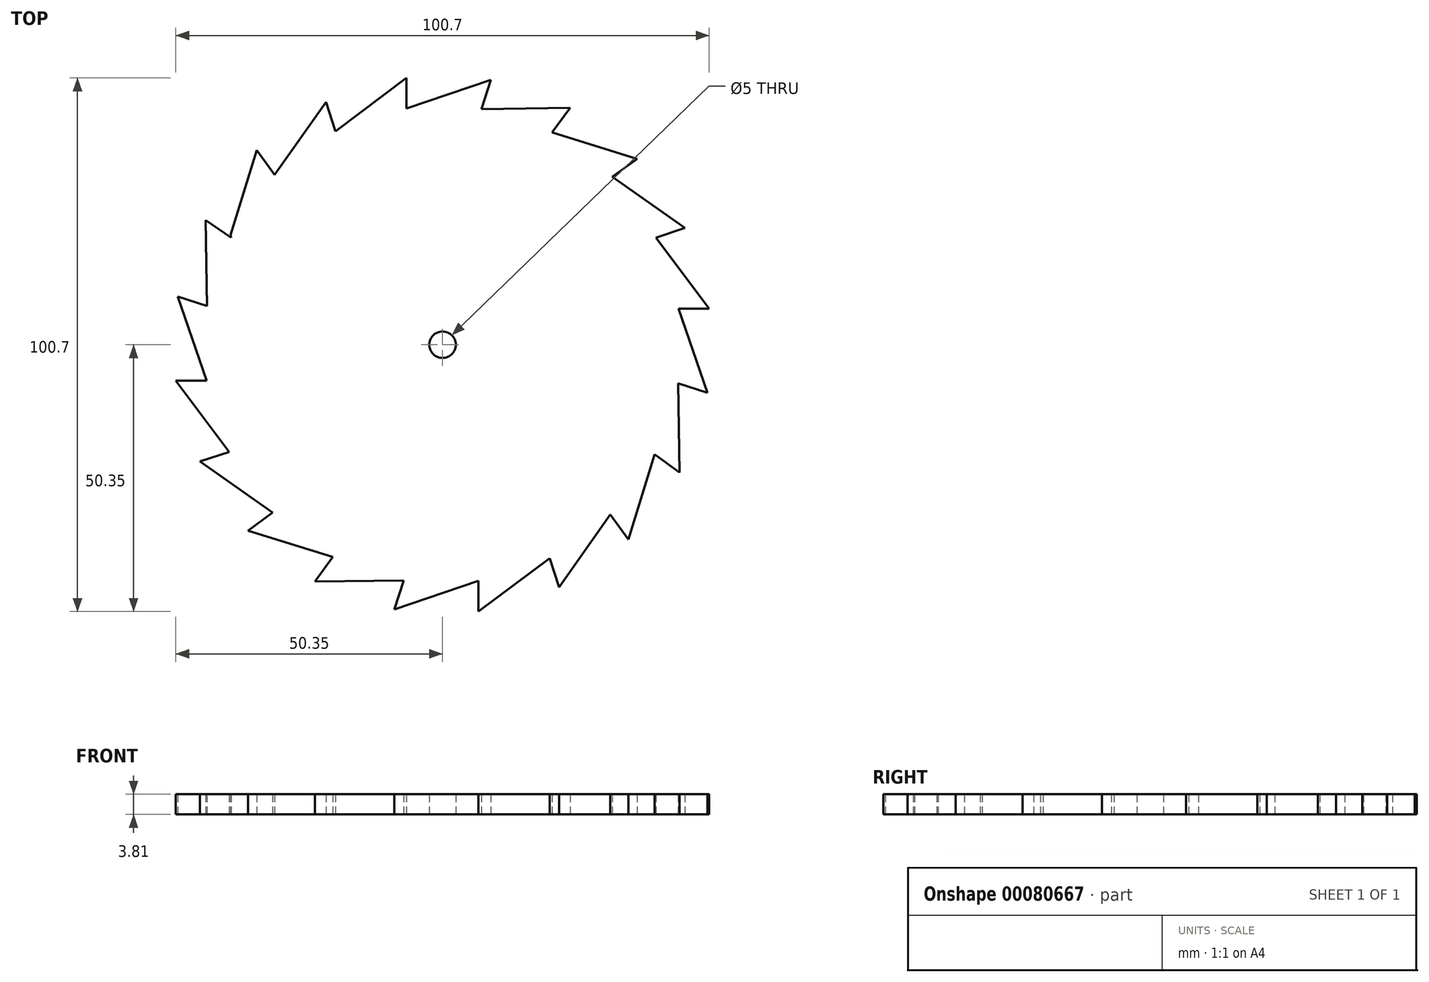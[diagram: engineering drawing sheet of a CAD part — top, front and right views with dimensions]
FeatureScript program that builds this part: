
annotation { "Feature Type Name" : "Feature", "Feature Type Description" : "" }
export const myFeature = defineFeature(function(context is Context, id is Id, definition is map)
    precondition{}
    {
        {
            var Q0;
            Q0=qCreatedBy(makeId("Top.planeOp"),FACE);
            var sketch = newSketch(context, id + "F0", { "sketchPlane" : qUnion([Q0])});
            skCircle(sketch, "E0", {"center": v(0, 0) * mm, "radius": 2.5 * mm});
            skCircle(sketch, "E1", {"center": v(0, 0) * mm, "radius": 8.48 * mm});
            skArc(sketch, "E2", {"start": v(-36.74, -35.09) * mm, "mid": v(-32.76, -38.83) * mm, "end": v(-28.4, -42.13) * mm});
            skLineSegment(sketch, "E3", {"start": v(0, 50.8) * mm, "end": v(-6.8, 44.57) * mm});
            skLineSegment(sketch, "E4", {"start": v(-6.8, 44.57) * mm, "end": v(-6.8, 50.35) * mm});
            skLineSegment(sketch, "E5.1.0", {"start": v(-17.4, 47.73) * mm, "end": v(-20.23, 40.29) * mm});
            skLineSegment(sketch, "E5.1.2", {"start": v(-20.23, 40.29) * mm, "end": v(-22.02, 45.78) * mm});
            skLineSegment(sketch, "E5.2.0", {"start": v(-31.3, 40.02) * mm, "end": v(-31.7, 32.06) * mm});
            skLineSegment(sketch, "E5.2.2", {"start": v(-31.7, 32.06) * mm, "end": v(-35.09, 36.74) * mm});
            skLineSegment(sketch, "E5.3.0", {"start": v(-42.13, 28.4) * mm, "end": v(-39.92, 20.21) * mm});
            skLineSegment(sketch, "E5.3.2", {"start": v(-39.92, 20.21) * mm, "end": v(-44.95, 23.67) * mm});
            skLineSegment(sketch, "E5.4.0", {"start": v(-48.84, 13.99) * mm, "end": v(-44.48, 7.31) * mm});
            skLineSegment(sketch, "E5.4.2", {"start": v(-44.48, 7.31) * mm, "end": v(-49.98, 9.1) * mm});
            skLineSegment(sketch, "E5.5.0", {"start": v(-50.77, -1.8) * mm, "end": v(-44.57, -6.8) * mm});
            skLineSegment(sketch, "E5.5.2", {"start": v(-44.57, -6.8) * mm, "end": v(-50.35, -6.8) * mm});
            skLineSegment(sketch, "E5.6.0", {"start": v(-47.73, -17.4) * mm, "end": v(-40.29, -20.23) * mm});
            skLineSegment(sketch, "E5.6.2", {"start": v(-40.29, -20.23) * mm, "end": v(-45.78, -22.02) * mm});
            skLineSegment(sketch, "E5.7.0", {"start": v(-40.02, -31.3) * mm, "end": v(-32.06, -31.7) * mm});
            skLineSegment(sketch, "E5.7.2", {"start": v(-32.06, -31.7) * mm, "end": v(-36.74, -35.09) * mm});
            skLineSegment(sketch, "E5.8.0", {"start": v(-28.4, -42.13) * mm, "end": v(-20.7, -40.05) * mm});
            skLineSegment(sketch, "E5.8.2", {"start": v(-20.7, -40.05) * mm, "end": v(-24.1, -44.72) * mm});
            skLineSegment(sketch, "E5.9.0", {"start": v(-13.99, -48.84) * mm, "end": v(-7.31, -44.48) * mm});
            skLineSegment(sketch, "E5.9.2", {"start": v(-7.31, -44.48) * mm, "end": v(-9.1, -49.98) * mm});
            skLineSegment(sketch, "E5.10.0", {"start": v(1.8, -50.77) * mm, "end": v(6.8, -44.57) * mm});
            skLineSegment(sketch, "E5.10.2", {"start": v(6.8, -44.57) * mm, "end": v(6.8, -50.35) * mm});
            skLineSegment(sketch, "E5.11.0", {"start": v(17.4, -47.73) * mm, "end": v(20.23, -40.29) * mm});
            skLineSegment(sketch, "E5.11.2", {"start": v(20.23, -40.29) * mm, "end": v(22.02, -45.78) * mm});
            skLineSegment(sketch, "E5.12.0", {"start": v(31.3, -40.02) * mm, "end": v(31.7, -32.06) * mm});
            skLineSegment(sketch, "E5.12.2", {"start": v(31.7, -32.06) * mm, "end": v(35.09, -36.74) * mm});
            skLineSegment(sketch, "E5.13.0", {"start": v(42.13, -28.4) * mm, "end": v(40.05, -20.7) * mm});
            skLineSegment(sketch, "E5.13.2", {"start": v(40.05, -20.7) * mm, "end": v(44.72, -24.1) * mm});
            skLineSegment(sketch, "E5.14.0", {"start": v(48.84, -13.99) * mm, "end": v(44.48, -7.31) * mm});
            skLineSegment(sketch, "E5.14.2", {"start": v(44.48, -7.31) * mm, "end": v(49.98, -9.1) * mm});
            skLineSegment(sketch, "E5.15.0", {"start": v(50.77, 1.8) * mm, "end": v(44.57, 6.8) * mm});
            skLineSegment(sketch, "E5.15.2", {"start": v(44.57, 6.8) * mm, "end": v(50.35, 6.8) * mm});
            skLineSegment(sketch, "E5.16.0", {"start": v(47.73, 17.4) * mm, "end": v(40.29, 20.23) * mm});
            skLineSegment(sketch, "E5.16.2", {"start": v(40.29, 20.23) * mm, "end": v(45.78, 22.02) * mm});
            skLineSegment(sketch, "E5.17.0", {"start": v(40.02, 31.3) * mm, "end": v(32.06, 31.7) * mm});
            skLineSegment(sketch, "E5.17.2", {"start": v(32.06, 31.7) * mm, "end": v(36.74, 35.09) * mm});
            skLineSegment(sketch, "E5.18.0", {"start": v(28.4, 42.13) * mm, "end": v(20.7, 40.05) * mm});
            skLineSegment(sketch, "E5.18.2", {"start": v(20.7, 40.05) * mm, "end": v(24.1, 44.72) * mm});
            skLineSegment(sketch, "E5.19.0", {"start": v(13.99, 48.84) * mm, "end": v(7.31, 44.48) * mm});
            skLineSegment(sketch, "E5.19.2", {"start": v(7.31, 44.48) * mm, "end": v(9.1, 49.98) * mm});
            skArc(sketch, "E6.trimOffspring", {"start": v(-9.1, -49.98) * mm, "mid": v(-3.67, -50.67) * mm, "end": v(1.8, -50.77) * mm});
            skArc(sketch, "E7.trimOffspring", {"start": v(-24.1, -44.72) * mm, "mid": v(-19.15, -47.06) * mm, "end": v(-13.99, -48.84) * mm});
            skArc(sketch, "E8.trimOffspring", {"start": v(-6.8, 50.35) * mm, "mid": v(-12.16, 49.33) * mm, "end": v(-17.4, 47.73) * mm});
            skArc(sketch, "E9.trimOffspring", {"start": v(-22.02, 45.78) * mm, "mid": v(-26.81, 43.15) * mm, "end": v(-31.3, 40.02) * mm});
            skArc(sketch, "E10.trimOffspring", {"start": v(-35.09, 36.74) * mm, "mid": v(-38.83, 32.76) * mm, "end": v(-42.13, 28.4) * mm});
            skArc(sketch, "E11.trimOffspring", {"start": v(-44.95, 23.67) * mm, "mid": v(-47.15, 18.93) * mm, "end": v(-48.84, 13.99) * mm});
            skArc(sketch, "E12.trimOffspring", {"start": v(-49.98, 9.1) * mm, "mid": v(-50.67, 3.67) * mm, "end": v(-50.77, -1.8) * mm});
            skArc(sketch, "E13.trimOffspring", {"start": v(-50.35, -6.8) * mm, "mid": v(-49.33, -12.16) * mm, "end": v(-47.73, -17.4) * mm});
            skArc(sketch, "E14.trimOffspring", {"start": v(-45.78, -22.02) * mm, "mid": v(-43.15, -26.81) * mm, "end": v(-40.02, -31.3) * mm});
            skArc(sketch, "E15.trimOffspring", {"start": v(6.8, -50.35) * mm, "mid": v(12.16, -49.33) * mm, "end": v(17.4, -47.73) * mm});
            skArc(sketch, "E16.trimOffspring", {"start": v(22.02, -45.78) * mm, "mid": v(26.81, -43.15) * mm, "end": v(31.3, -40.02) * mm});
            skArc(sketch, "E17.trimOffspring", {"start": v(35.09, -36.74) * mm, "mid": v(38.83, -32.76) * mm, "end": v(42.13, -28.4) * mm});
            skArc(sketch, "E18.trimOffspring", {"start": v(44.72, -24.1) * mm, "mid": v(47.06, -19.15) * mm, "end": v(48.84, -13.99) * mm});
            skArc(sketch, "E19.trimOffspring", {"start": v(49.98, -9.1) * mm, "mid": v(50.67, -3.67) * mm, "end": v(50.77, 1.8) * mm});
            skArc(sketch, "E20.trimOffspring", {"start": v(50.35, 6.8) * mm, "mid": v(49.33, 12.16) * mm, "end": v(47.73, 17.4) * mm});
            skArc(sketch, "E21.trimOffspring", {"start": v(45.78, 22.02) * mm, "mid": v(43.15, 26.81) * mm, "end": v(40.02, 31.3) * mm});
            skArc(sketch, "E22.trimOffspring", {"start": v(36.74, 35.09) * mm, "mid": v(32.76, 38.83) * mm, "end": v(28.4, 42.13) * mm});
            skArc(sketch, "E23.trimOffspring", {"start": v(24.1, 44.72) * mm, "mid": v(19.15, 47.06) * mm, "end": v(13.99, 48.84) * mm});
            skArc(sketch, "E24.trimOffspring", {"start": v(9.1, 49.98) * mm, "mid": v(4.57, 50.6) * mm, "end": v(0, 50.8) * mm});
            skPoint(sketch, "E25.orphan", {"position": v(-5.14, -35.84) * mm});
            skPoint(sketch, "E26.orphan", {"position": v(6.8, -32.02) * mm});
            skPoint(sketch, "E27.orphan", {"position": v(16.9, -32.02) * mm});
            skPoint(sketch, "E28.orphan", {"position": v(25.97, -25.23) * mm});
            skPoint(sketch, "E29.orphan", {"position": v(32.5, -15.97) * mm});
            skPoint(sketch, "E30.orphan", {"position": v(35.84, -5.14) * mm});
            skPoint(sketch, "E31.orphan", {"position": v(-29.9, 13.33) * mm});
            skPoint(sketch, "E32.orphan", {"position": v(-24.32, 21.91) * mm});
            skPoint(sketch, "E33.orphan", {"position": v(-16.35, 28.35) * mm});
            skPoint(sketch, "E34.orphan", {"position": v(-6.8, 32.02) * mm});
            skPoint(sketch, "E35.orphan", {"position": v(13.33, 29.9) * mm});
            skPoint(sketch, "E36.orphan", {"position": v(35.68, 6.18) * mm});
            skPoint(sketch, "E37.orphan", {"position": v(32.02, 16.9) * mm});
            skLineSegment(sketch, "E38", {"start": v(-22.02, 45.78) * mm, "end": v(-31.7, 32.06) * mm});
            skLineSegment(sketch, "E39.1.0", {"start": v(-35.09, 36.74) * mm, "end": v(-40.05, 20.7) * mm});
            skLineSegment(sketch, "E39.2.0", {"start": v(-44.72, 24.1) * mm, "end": v(-44.48, 7.31) * mm});
            skLineSegment(sketch, "E39.3.0", {"start": v(-49.98, 9.1) * mm, "end": v(-44.57, -6.8) * mm});
            skLineSegment(sketch, "E39.4.0", {"start": v(-50.35, -6.8) * mm, "end": v(-40.29, -20.23) * mm});
            skLineSegment(sketch, "E39.5.0", {"start": v(-45.78, -22.02) * mm, "end": v(-32.06, -31.7) * mm});
            skLineSegment(sketch, "E39.6.0", {"start": v(-36.74, -35.09) * mm, "end": v(-20.7, -40.05) * mm});
            skLineSegment(sketch, "E39.7.0", {"start": v(-24.1, -44.72) * mm, "end": v(-7.31, -44.48) * mm});
            skLineSegment(sketch, "E39.8.0", {"start": v(-9.1, -49.98) * mm, "end": v(6.8, -44.57) * mm});
            skLineSegment(sketch, "E39.9.0", {"start": v(6.8, -50.35) * mm, "end": v(20.23, -40.29) * mm});
            skLineSegment(sketch, "E39.10.0", {"start": v(22.02, -45.78) * mm, "end": v(31.7, -32.06) * mm});
            skLineSegment(sketch, "E39.11.0", {"start": v(35.09, -36.74) * mm, "end": v(40.05, -20.7) * mm});
            skLineSegment(sketch, "E39.12.0", {"start": v(44.72, -24.1) * mm, "end": v(44.48, -7.31) * mm});
            skLineSegment(sketch, "E39.13.0", {"start": v(49.98, -9.1) * mm, "end": v(44.57, 6.8) * mm});
            skLineSegment(sketch, "E39.14.0", {"start": v(50.35, 6.8) * mm, "end": v(40.29, 20.23) * mm});
            skLineSegment(sketch, "E39.15.0", {"start": v(45.78, 22.02) * mm, "end": v(32.06, 31.7) * mm});
            skLineSegment(sketch, "E39.16.0", {"start": v(36.74, 35.09) * mm, "end": v(20.7, 40.05) * mm});
            skLineSegment(sketch, "E39.17.0", {"start": v(24.1, 44.72) * mm, "end": v(7.31, 44.48) * mm});
            skLineSegment(sketch, "E39.18.0", {"start": v(9.1, 49.98) * mm, "end": v(-6.8, 44.57) * mm});
            skLineSegment(sketch, "E39.19.0", {"start": v(-6.8, 50.35) * mm, "end": v(-20.23, 40.29) * mm});
            skSolve(sketch);
        }
        {
            var Q0;
            Q0=makeQuery(id+"F0.imprint","IMPRINT",FACE,{"disambiguationData":[TD([[makeQuery(id+"F0.imprint","IMPRINT",EDGE,{"derivedFrom":sQuery(id+"F0.wireOp",EDGE,"E1")}),-1.0]])]});
            var Q1;
            Q1=makeQuery(id+"F0.imprint","IMPRINT",FACE,{"disambiguationData":[TD([[makeQuery(id+"F0.imprint","IMPRINT",EDGE,{"derivedFrom":sQuery(id+"F0.wireOp",EDGE,"E0")}),-1.0]])]});
            extrude(context, id + "F1", {"entities" : qUnion([Q0, Q1]), "depth" : 3.81 * mm});
        }
    });
